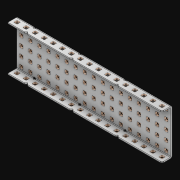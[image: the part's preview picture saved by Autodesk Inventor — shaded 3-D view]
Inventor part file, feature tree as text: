
AUTODESK INVENTOR PART (.ipt)
format: ipt  version: 2021 (Build 250183000, 183)  size: 3,289,600 bytes
history: native  units: in
note: dims shown in document units (in); Inventor stores cm internally (conversion verified against a paired STEP export)
features: extrude x120, other x119, sketch x4, thicken_offset x3, pattern_linear x3, imported_body x1
ambient origin geometry x8: Origin, YZ Plane, XZ Plane, XY Plane, X Axis, Y Axis, Z Axis, Center Point
bodies: Solid1 (feature_tree)
feature tree (250):
  thicken_offset  "Thicken1"
  thicken_offset  "Thicken2"
  thicken_offset  "Thicken3"
  pattern_linear  "Rectangular Pattern1"  Spacing1=0.001in  [1 undecoded]
  pattern_linear  "Rectangular Pattern2"  Spacing1=0.001in  [1 undecoded]
  pattern_linear  "Rectangular Pattern3"  Spacing1=0.182in  [1 undecoded]
  extrude  "Extrusion1"  Depth=0.063in TaperAngle=0.0deg
  sketch  "Sketch1"  dims[d0=0.001in]
  other  "Srf1"
  sketch  "Sketch2"  dims[d1=0.001in]
  other  "Srf2"
  sketch  "Sketch3"  dims[d2=0.001in]
  other  "Srf3"
  other  "Srf4"
  other  "Srf5"
  other  "Srf6"
  other  "Srf7"
  other  "Srf8"
  other  "Srf9"
  other  "Srf10"
  other  "Srf11"
  other  "Srf12"
  other  "Srf13"
  other  "Srf14"
  other  "Srf15"
  other  "Srf16"
  other  "Srf17"
  other  "Srf18"
  other  "Srf19"
  other  "Srf38"
  other  "Srf39"
  other  "Srf40"
  other  "Srf41"
  other  "Srf42"
  other  "Srf43"
  other  "Srf44"
  other  "Srf45"
  other  "Srf46"
  other  "Srf47"
  other  "Srf48"
  other  "Srf49"
  other  "Srf50"
  other  "Srf51"
  other  "Srf52"
  other  "Srf53"
  other  "Srf72"
  other  "Srf73"
  other  "Srf74"
  other  "Srf75"
  other  "Srf76"
  other  "Srf77"
  other  "Srf78"
  other  "Srf79"
  other  "Srf80"
  other  "Srf81"
  other  "Srf82"
  other  "Srf83"
  other  "Srf84"
  other  "Srf85"
  other  "Srf86"
  other  "Srf87"
  other  "Srf106"
  other  "Srf107"
  other  "Srf108"
  other  "Srf109"
  other  "Srf110"
  other  "Srf111"
  other  "Srf112"
  other  "Srf113"
  other  "Srf114"
  other  "Srf115"
  other  "Srf116"
  other  "Srf117"
  other  "Srf118"
  other  "Srf119"
  other  "Srf120"
  other  "Srf121"
  other  "Srf122"
  other  "Srf141"
  other  "Srf142"
  other  "Srf143"
  other  "Srf144"
  other  "Srf145"
  other  "Srf146"
  other  "Srf147"
  other  "Srf148"
  other  "Srf149"
  other  "Srf150"
  other  "Srf151"
  other  "Srf152"
  other  "Srf153"
  other  "Srf154"
  other  "Srf155"
  other  "Srf156"
  other  "Srf157"
  other  "Srf176"
  other  "Srf177"
  other  "Srf178"
  other  "Srf179"
  other  "Srf180"
  other  "Srf181"
  other  "Srf182"
  other  "Srf183"
  other  "Srf184"
  other  "Srf185"
  other  "Srf186"
  other  "Srf187"
  other  "Srf188"
  other  "Srf189"
  other  "Srf190"
  other  "Srf191"
  other  "Srf192"
  other  "Srf211"
  other  "Srf212"
  other  "Srf213"
  other  "Srf214"
  other  "Srf215"
  other  "Srf216"
  other  "Srf217"
  other  "Srf218"
  other  "Srf219"
  other  "Srf220"
  other  "Srf221"
  other  "Srf222"
  other  "Srf223"
  other  "Srf224"
  other  "Srf225"
  other  "Srf226"
  other  "Srf227"
  sketch  "Sketch4"  dims[d3=0.001in d4=0.001in d5=0.001in d6=0.182in d7=0.063in d8=0.0in d9=0.182in d10=0.063in d11=0.0in d12=0.182in d13=0.063in d14=0.0in d17=0.5in d18=6.6929in d20=0.5in d21=6.6929in d23=0.5in d24=1.9685in d26=0.5in d27=9.0in d28=0.0in]
  imported_body  "Imported1"
  extrude  "ExtrusionSrf1"  Depth=0.5in
  extrude  "ExtrusionSrf2"  Depth=0.063in TaperAngle=0.0deg
  extrude  "ExtrusionSrf3"  Depth=0.5in
  extrude  "ExtrusionSrf4"  Depth=0.063in TaperAngle=0.0deg
  extrude  "ExtrusionSrf5"  Depth=0.5in
  extrude  "ExtrusionSrf6"  Depth=0.5in
  extrude  "ExtrusionSrf7"  Depth=0.5in
  extrude  "ExtrusionSrf8"  Depth=0.5in
  extrude  "ExtrusionSrf9"  Depth=0.5in
  extrude  "ExtrusionSrf10"  Depth=0.5in
  extrude  "ExtrusionSrf11"  Depth=0.5in
  extrude  "ExtrusionSrf12"  TaperAngle=0.0deg  [1 undecoded]
  extrude  "ExtrusionSrf13"  [1 undecoded]
  extrude  "ExtrusionSrf14"  [1 undecoded]
  extrude  "ExtrusionSrf15"  [1 undecoded]
  extrude  "ExtrusionSrf16"  [1 undecoded]
  extrude  "ExtrusionSrf17"  [1 undecoded]
  extrude  "ExtrusionSrf18"  [1 undecoded]
  extrude  "ExtrusionSrf19"  [1 undecoded]
  extrude  "ExtrusionSrf38"  [1 undecoded]
  extrude  "ExtrusionSrf39"  [1 undecoded]
  extrude  "ExtrusionSrf40"  [1 undecoded]
  extrude  "ExtrusionSrf41"  [1 undecoded]
  extrude  "ExtrusionSrf42"  [1 undecoded]
  extrude  "ExtrusionSrf43"  [1 undecoded]
  extrude  "ExtrusionSrf44"  [1 undecoded]
  extrude  "ExtrusionSrf45"  [1 undecoded]
  extrude  "ExtrusionSrf46"  [1 undecoded]
  extrude  "ExtrusionSrf47"  [1 undecoded]
  extrude  "ExtrusionSrf48"  [1 undecoded]
  extrude  "ExtrusionSrf49"  [1 undecoded]
  extrude  "ExtrusionSrf50"  [1 undecoded]
  extrude  "ExtrusionSrf51"  [1 undecoded]
  extrude  "ExtrusionSrf52"  [1 undecoded]
  extrude  "ExtrusionSrf53"  [1 undecoded]
  extrude  "ExtrusionSrf72"  [1 undecoded]
  extrude  "ExtrusionSrf73"  [1 undecoded]
  extrude  "ExtrusionSrf74"  [1 undecoded]
  extrude  "ExtrusionSrf75"  [1 undecoded]
  extrude  "ExtrusionSrf76"  [1 undecoded]
  extrude  "ExtrusionSrf77"  [1 undecoded]
  extrude  "ExtrusionSrf78"  [1 undecoded]
  extrude  "ExtrusionSrf79"  [1 undecoded]
  extrude  "ExtrusionSrf80"  [1 undecoded]
  extrude  "ExtrusionSrf81"  [1 undecoded]
  extrude  "ExtrusionSrf82"  [1 undecoded]
  extrude  "ExtrusionSrf83"  [1 undecoded]
  extrude  "ExtrusionSrf84"  [1 undecoded]
  extrude  "ExtrusionSrf85"  [1 undecoded]
  extrude  "ExtrusionSrf86"  [1 undecoded]
  extrude  "ExtrusionSrf87"  [1 undecoded]
  extrude  "ExtrusionSrf106"  [1 undecoded]
  extrude  "ExtrusionSrf107"  [1 undecoded]
  extrude  "ExtrusionSrf108"  [1 undecoded]
  extrude  "ExtrusionSrf109"  [1 undecoded]
  extrude  "ExtrusionSrf110"  [1 undecoded]
  extrude  "ExtrusionSrf111"  [1 undecoded]
  extrude  "ExtrusionSrf112"  [1 undecoded]
  extrude  "ExtrusionSrf113"  [1 undecoded]
  extrude  "ExtrusionSrf114"  [1 undecoded]
  extrude  "ExtrusionSrf115"  [1 undecoded]
  extrude  "ExtrusionSrf116"  [1 undecoded]
  extrude  "ExtrusionSrf117"  [1 undecoded]
  extrude  "ExtrusionSrf118"  [1 undecoded]
  extrude  "ExtrusionSrf119"  [1 undecoded]
  extrude  "ExtrusionSrf120"  [1 undecoded]
  extrude  "ExtrusionSrf121"  [1 undecoded]
  extrude  "ExtrusionSrf122"  [1 undecoded]
  extrude  "ExtrusionSrf141"  [1 undecoded]
  extrude  "ExtrusionSrf142"  [1 undecoded]
  extrude  "ExtrusionSrf143"  [1 undecoded]
  extrude  "ExtrusionSrf144"  [1 undecoded]
  extrude  "ExtrusionSrf145"  [1 undecoded]
  extrude  "ExtrusionSrf146"  [1 undecoded]
  extrude  "ExtrusionSrf147"  [1 undecoded]
  extrude  "ExtrusionSrf148"  [1 undecoded]
  extrude  "ExtrusionSrf149"  [1 undecoded]
  extrude  "ExtrusionSrf150"  [1 undecoded]
  extrude  "ExtrusionSrf151"  [1 undecoded]
  extrude  "ExtrusionSrf152"  [1 undecoded]
  extrude  "ExtrusionSrf153"  [1 undecoded]
  extrude  "ExtrusionSrf154"  [1 undecoded]
  extrude  "ExtrusionSrf155"  [1 undecoded]
  extrude  "ExtrusionSrf156"  [1 undecoded]
  extrude  "ExtrusionSrf157"  [1 undecoded]
  extrude  "ExtrusionSrf176"  [1 undecoded]
  extrude  "ExtrusionSrf177"  [1 undecoded]
  extrude  "ExtrusionSrf178"  [1 undecoded]
  extrude  "ExtrusionSrf179"  [1 undecoded]
  extrude  "ExtrusionSrf180"  [1 undecoded]
  extrude  "ExtrusionSrf181"  [1 undecoded]
  extrude  "ExtrusionSrf182"  [1 undecoded]
  extrude  "ExtrusionSrf183"  [1 undecoded]
  extrude  "ExtrusionSrf184"  [1 undecoded]
  extrude  "ExtrusionSrf185"  [1 undecoded]
  extrude  "ExtrusionSrf186"  [1 undecoded]
  extrude  "ExtrusionSrf187"  [1 undecoded]
  extrude  "ExtrusionSrf188"  [1 undecoded]
  extrude  "ExtrusionSrf189"  [1 undecoded]
  extrude  "ExtrusionSrf190"  [1 undecoded]
  extrude  "ExtrusionSrf191"  [1 undecoded]
  extrude  "ExtrusionSrf192"  [1 undecoded]
  extrude  "ExtrusionSrf211"  [1 undecoded]
  extrude  "ExtrusionSrf212"  [1 undecoded]
  extrude  "ExtrusionSrf213"  [1 undecoded]
  extrude  "ExtrusionSrf214"  [1 undecoded]
  extrude  "ExtrusionSrf215"  [1 undecoded]
  extrude  "ExtrusionSrf216"  [1 undecoded]
  extrude  "ExtrusionSrf217"  [1 undecoded]
  extrude  "ExtrusionSrf218"  [1 undecoded]
  extrude  "ExtrusionSrf219"  [1 undecoded]
  extrude  "ExtrusionSrf220"  [1 undecoded]
  extrude  "ExtrusionSrf221"  [1 undecoded]
  extrude  "ExtrusionSrf222"  [1 undecoded]
  extrude  "ExtrusionSrf223"  [1 undecoded]
  extrude  "ExtrusionSrf224"  [1 undecoded]
  extrude  "ExtrusionSrf225"  [1 undecoded]
  extrude  "ExtrusionSrf226"  [1 undecoded]
  extrude  "ExtrusionSrf227"  [1 undecoded]
note: 111 required parameter values undecoded (feature->parameter linkage not recoverable at this tier; creation-order binding heuristic only, values carry confidence <= 0.55)
